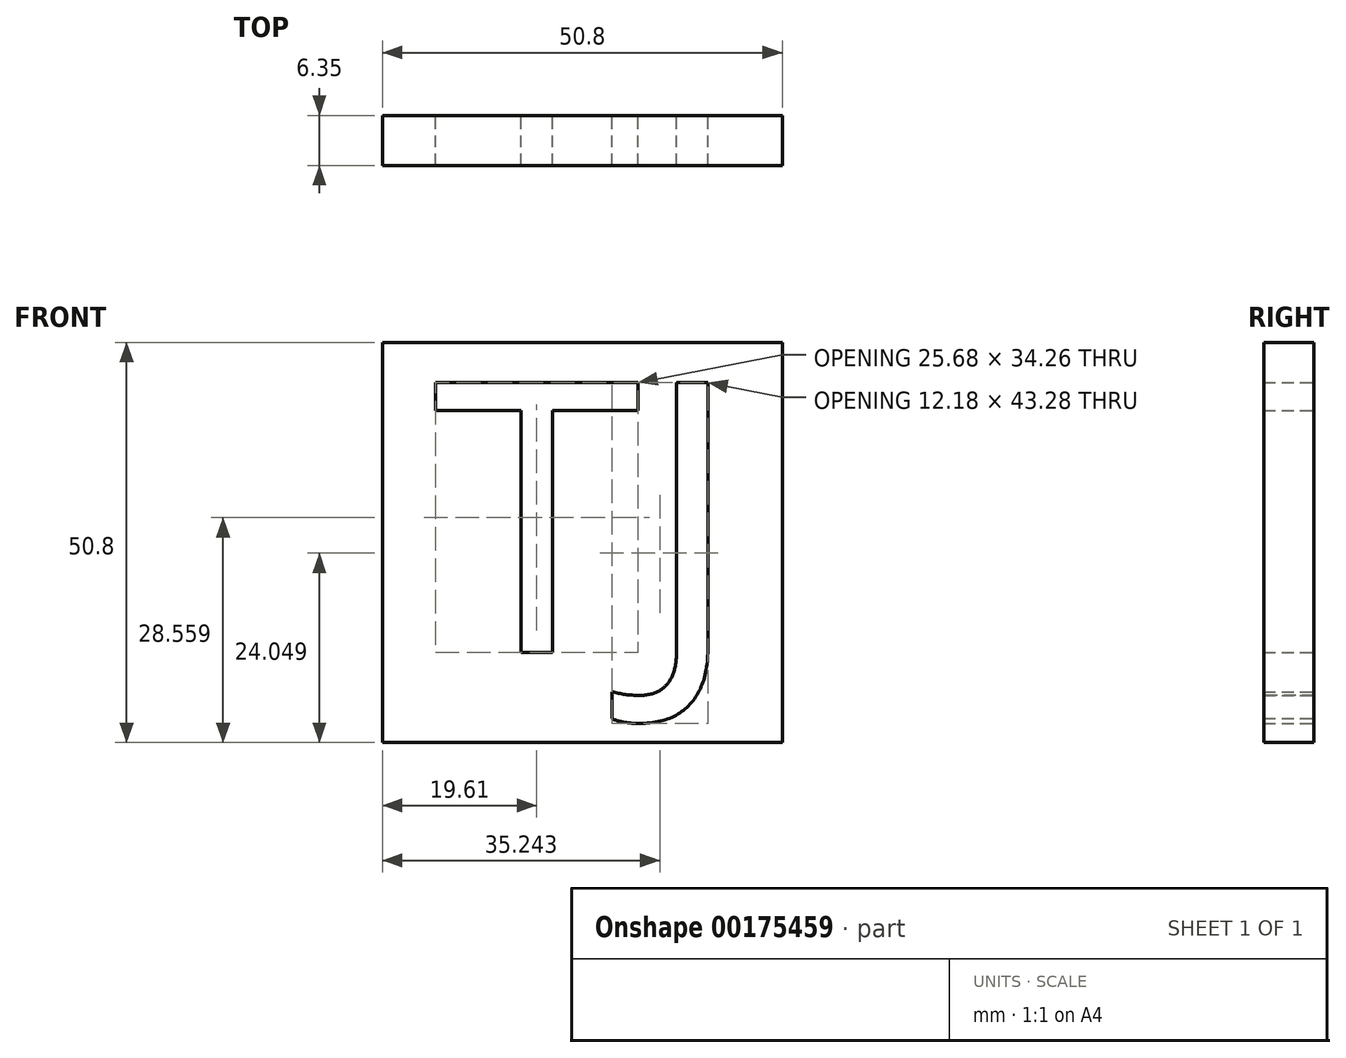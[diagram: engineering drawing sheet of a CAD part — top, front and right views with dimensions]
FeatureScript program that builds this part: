
annotation { "Feature Type Name" : "Feature", "Feature Type Description" : "" }
export const myFeature = defineFeature(function(context is Context, id is Id, definition is map)
    precondition{}
    {
        {
            var Q0;
            Q0=qCreatedBy(makeId("Front.planeOp"),FACE);
            var sketch = newSketch(context, id + "F0", { "sketchPlane" : qUnion([Q0])});
            skLineSegment(sketch, "E0.bottom", {"start": v(12.1, 43.96) * mm, "end": v(62.9, 43.96) * mm});
            skLineSegment(sketch, "E0.top", {"start": v(12.1, -6.84) * mm, "end": v(62.9, -6.84) * mm});
            skLineSegment(sketch, "E0.left", {"start": v(12.1, 43.96) * mm, "end": v(12.1, -6.84) * mm});
            skLineSegment(sketch, "E0.right", {"start": v(62.9, 43.96) * mm, "end": v(62.9, -6.84) * mm});
            skText(sketch, "E1", { "text": "TJ", "fontName": "OpenSans-Regular.ttf"});
            skPoint(sketch, "E2", {"position": v(-101.09, 60.87) * mm});
            const initialGuessF0  = {"E1": [0.01846, 0.00459, 1, 0, 0.03455]};
            skSetInitialGuess(sketch, initialGuessF0);
            skSolve(sketch);
        }
        {
            var Q0;
            Q0=makeQuery(id+"F0.imprint","IMPRINT",FACE,{"disambiguationData":[TD([[makeQuery(id+"F0.imprint","IMPRINT",EDGE,{"derivedFrom":sQuery(id+"F0.wireOp",EDGE,"E0.bottom")}),-1.0]])]});
            extrude(context, id + "F1", {"entities" : qUnion([Q0]), "depth" : 6.35 * mm});
        }
    });
